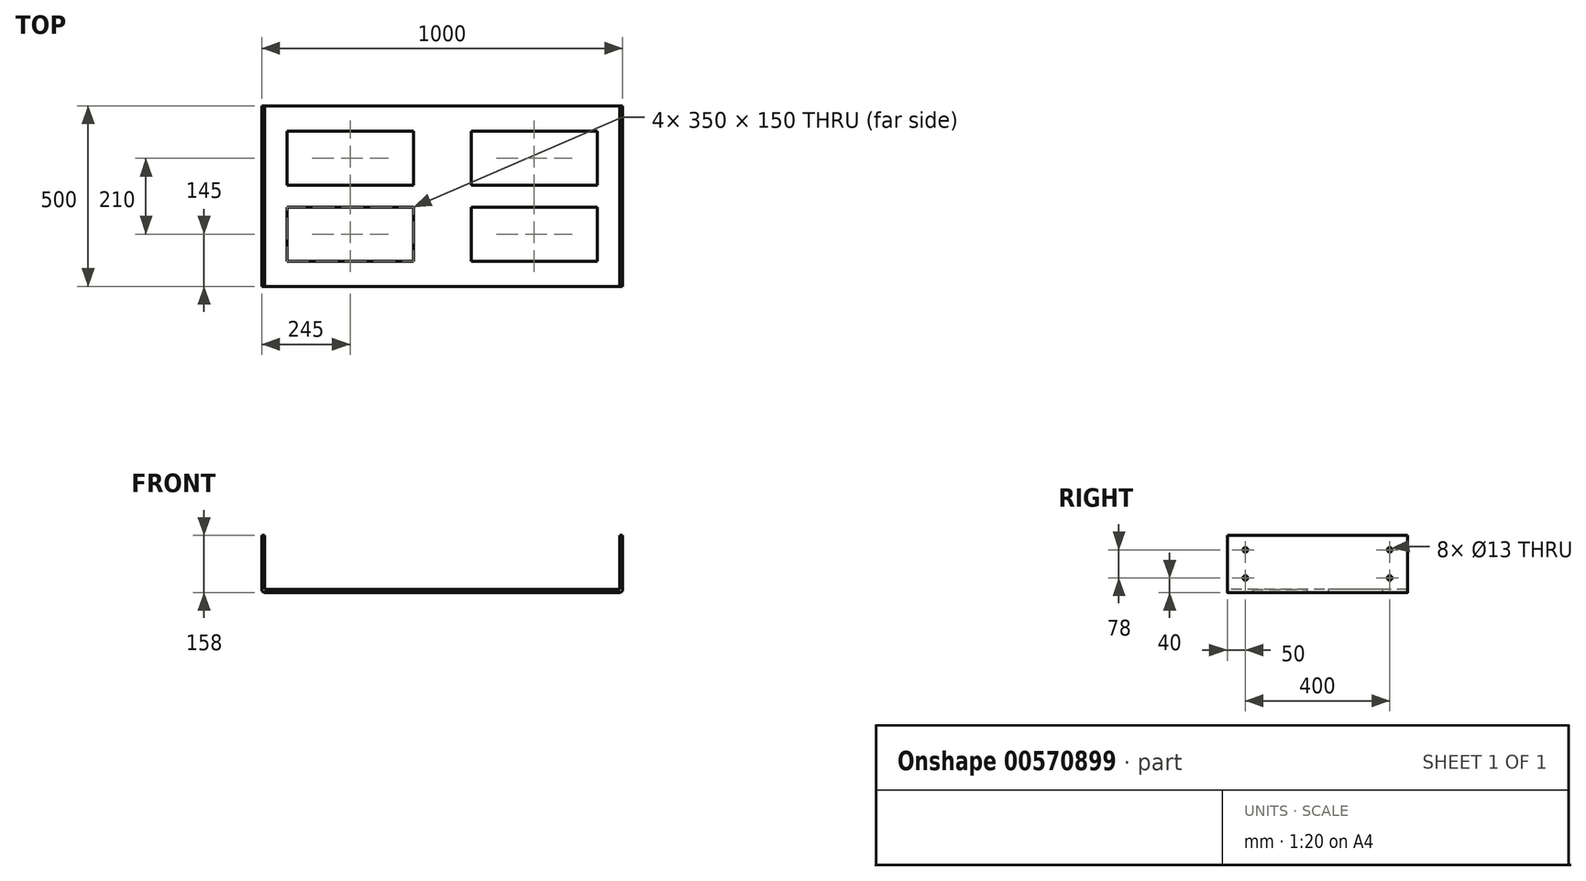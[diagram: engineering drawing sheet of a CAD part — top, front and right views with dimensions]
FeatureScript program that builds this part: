
annotation { "Feature Type Name" : "Feature", "Feature Type Description" : "" }
export const myFeature = defineFeature(function(context is Context, id is Id, definition is map)
    precondition{}
    {
        {
            var Q0;
            Q0=qCreatedBy(makeId("Top.planeOp"),FACE);
            var sketch = newSketch(context, id + "F0", { "sketchPlane" : qUnion([Q0])});
            skLineSegment(sketch, "E0.bottom", {"start": v(-500, 250) * mm, "end": v(500, 250) * mm});
            skLineSegment(sketch, "E0.top", {"start": v(-500, -250) * mm, "end": v(500, -250) * mm});
            skLineSegment(sketch, "E0.left", {"start": v(-500, 250) * mm, "end": v(-500, -250) * mm});
            skLineSegment(sketch, "E0.right", {"start": v(500, 250) * mm, "end": v(500, -250) * mm});
            skLineSegment(sketch, "E1.bottom", {"start": v(-430, 180) * mm, "end": v(-80, 180) * mm});
            skLineSegment(sketch, "E1.top", {"start": v(-430, 30) * mm, "end": v(-80, 30) * mm});
            skLineSegment(sketch, "E1.left", {"start": v(-430, 180) * mm, "end": v(-430, 30) * mm});
            skLineSegment(sketch, "E1.right", {"start": v(-80, 180) * mm, "end": v(-80, 30) * mm});
            skLineSegment(sketch, "E2.MirrorCS", {"start": v(80, 180) * mm, "end": v(80, 30) * mm});
            skLineSegment(sketch, "E3.MirrorCS", {"start": v(430, 180) * mm, "end": v(80, 180) * mm});
            skLineSegment(sketch, "E4.MirrorCS", {"start": v(430, 180) * mm, "end": v(430, 30) * mm});
            skLineSegment(sketch, "E5.MirrorCS", {"start": v(430, 30) * mm, "end": v(80, 30) * mm});
            skLineSegment(sketch, "E6.MirrorCS", {"start": v(-430, -30) * mm, "end": v(-80, -30) * mm});
            skLineSegment(sketch, "E7.MirrorCS", {"start": v(-80, -180) * mm, "end": v(-80, -30) * mm});
            skLineSegment(sketch, "E8.MirrorCS", {"start": v(-430, -180) * mm, "end": v(-430, -30) * mm});
            skLineSegment(sketch, "E9.MirrorCS", {"start": v(-430, -180) * mm, "end": v(-80, -180) * mm});
            skLineSegment(sketch, "E10.MirrorCS", {"start": v(430, -180) * mm, "end": v(80, -180) * mm});
            skLineSegment(sketch, "E11.MirrorCS", {"start": v(430, -180) * mm, "end": v(430, -30) * mm});
            skLineSegment(sketch, "E12.MirrorCS", {"start": v(80, -180) * mm, "end": v(80, -30) * mm});
            skLineSegment(sketch, "E13.MirrorCS", {"start": v(430, -30) * mm, "end": v(80, -30) * mm});
            skSolve(sketch);
        }
        {
            var Q0;
            Q0=makeQuery(id+"F0.imprint","IMPRINT",FACE,{"disambiguationData":[TD([[makeQuery(id+"F0.imprint","IMPRINT",EDGE,{"derivedFrom":sQuery(id+"F0.wireOp",EDGE,"E0.bottom")}),-1.0]])]});
            extrude(context, id + "F1", {"entities" : qUnion([Q0]), "depth" : 8 * mm, "offsetDistance" : 25 * mm});
        }
        {
            var Q0;
            Q0=makeQuery(id+"F1.opExtrude","CAP_FACE",FACE,{"disambiguationData":[OSD([sQuery(id+"F0.wireOp",EDGE,"E0.bottom"),sQuery(id+"F0.wireOp",EDGE,"E0.top"),sQuery(id+"F0.wireOp",EDGE,"E0.left"),sQuery(id+"F0.wireOp",EDGE,"E0.right"),sQuery(id+"F0.wireOp",EDGE,"E1.bottom"),sQuery(id+"F0.wireOp",EDGE,"E1.top"),sQuery(id+"F0.wireOp",EDGE,"E1.left"),sQuery(id+"F0.wireOp",EDGE,"E1.right"),sQuery(id+"F0.wireOp",EDGE,"E2.MirrorCS"),sQuery(id+"F0.wireOp",EDGE,"E3.MirrorCS"),sQuery(id+"F0.wireOp",EDGE,"E4.MirrorCS"),sQuery(id+"F0.wireOp",EDGE,"E5.MirrorCS"),sQuery(id+"F0.wireOp",EDGE,"E6.MirrorCS"),sQuery(id+"F0.wireOp",EDGE,"E7.MirrorCS"),sQuery(id+"F0.wireOp",EDGE,"E8.MirrorCS"),sQuery(id+"F0.wireOp",EDGE,"E9.MirrorCS"),sQuery(id+"F0.wireOp",EDGE,"E10.MirrorCS"),sQuery(id+"F0.wireOp",EDGE,"E11.MirrorCS"),sQuery(id+"F0.wireOp",EDGE,"E12.MirrorCS"),sQuery(id+"F0.wireOp",EDGE,"E13.MirrorCS")])],"isStart":false});
            var sketch = newSketch(context, id + "F2", { "sketchPlane" : qUnion([Q0])});
            skLineSegment(sketch, "E14.bottom", {"start": v(-500, -250) * mm, "end": v(-492, -250) * mm});
            skLineSegment(sketch, "E14.top", {"start": v(-500, 250) * mm, "end": v(-492, 250) * mm});
            skLineSegment(sketch, "E14.left", {"start": v(-500, -250) * mm, "end": v(-500, 250) * mm});
            skLineSegment(sketch, "E14.right", {"start": v(-492, -250) * mm, "end": v(-492, 250) * mm});
            skLineSegment(sketch, "E15.bottom", {"start": v(500, 250) * mm, "end": v(492, 250) * mm});
            skLineSegment(sketch, "E15.top", {"start": v(500, -250) * mm, "end": v(492, -250) * mm});
            skLineSegment(sketch, "E15.left", {"start": v(500, 250) * mm, "end": v(500, -250) * mm});
            skLineSegment(sketch, "E15.right", {"start": v(492, 250) * mm, "end": v(492, -250) * mm});
            skSolve(sketch);
        }
        {
            var Q0;
            Q0 = qSketchRegion(id + "F2", true);
            extrude(context, id + "F3", {"entities" : qUnion([Q0]), "operationType" : NewBodyOperationType.ADD, "depth" : 150 * mm, "offsetDistance" : 25 * mm});
        }
        {
            var Q0;
            Q0=makeQuery(id+"F1.opExtrude","CAP_EDGE",EDGE,{"disambiguationData":[OSD([sQuery(id+"F0.wireOp",EDGE,"E0.left")])],"isStart":true});
            var Q1;
            Q1=makeQuery(id+"F1.opExtrude","CAP_EDGE",EDGE,{"disambiguationData":[OSD([sQuery(id+"F0.wireOp",EDGE,"E0.right")])],"isStart":true});
            fillet(context, id + "F4", {"entities" : qUnion([Q0, Q1]), "radius" : 8 * mm, "tangentPropagation" : true, "allowEdgeOverflow" : false});
        }
        {
            var Q0;
            Q0=makeQuery(id+"F3.boolean.opBoolean","MERGE",FACE,{"derivedFrom":[makeQuery(id+"F1.opExtrude","SWEPT_FACE",FACE,{"disambiguationData":[OSD([sQuery(id+"F0.wireOp",EDGE,"E0.left")])]}),makeQuery(id+"F3.opExtrude","SWEPT_FACE",FACE,{"disambiguationData":[OSD([sQuery(id+"F2.wireOp",EDGE,"E14.left")])]})]});
            var sketch = newSketch(context, id + "F5", { "sketchPlane" : qUnion([Q0])});
            skCircle(sketch, "E16", {"center": v(-200, 40) * mm, "radius": 6.5 * mm});
            skCircle(sketch, "E17", {"center": v(-200, 118) * mm, "radius": 6.5 * mm});
            skCircle(sketch, "E18", {"center": v(200, 118) * mm, "radius": 6.5 * mm});
            skCircle(sketch, "E19", {"center": v(200, 40) * mm, "radius": 6.5 * mm});
            skSolve(sketch);
        }
        {
            var Q0;
            Q0 = qSketchRegion(id + "F5", true);
            extrude(context, id + "F6", {"entities" : qUnion([Q0]), "operationType" : NewBodyOperationType.REMOVE, "oppositeDirection" : true, "depth" : 1200 * mm, "offsetDistance" : 25 * mm});
        }
    });
